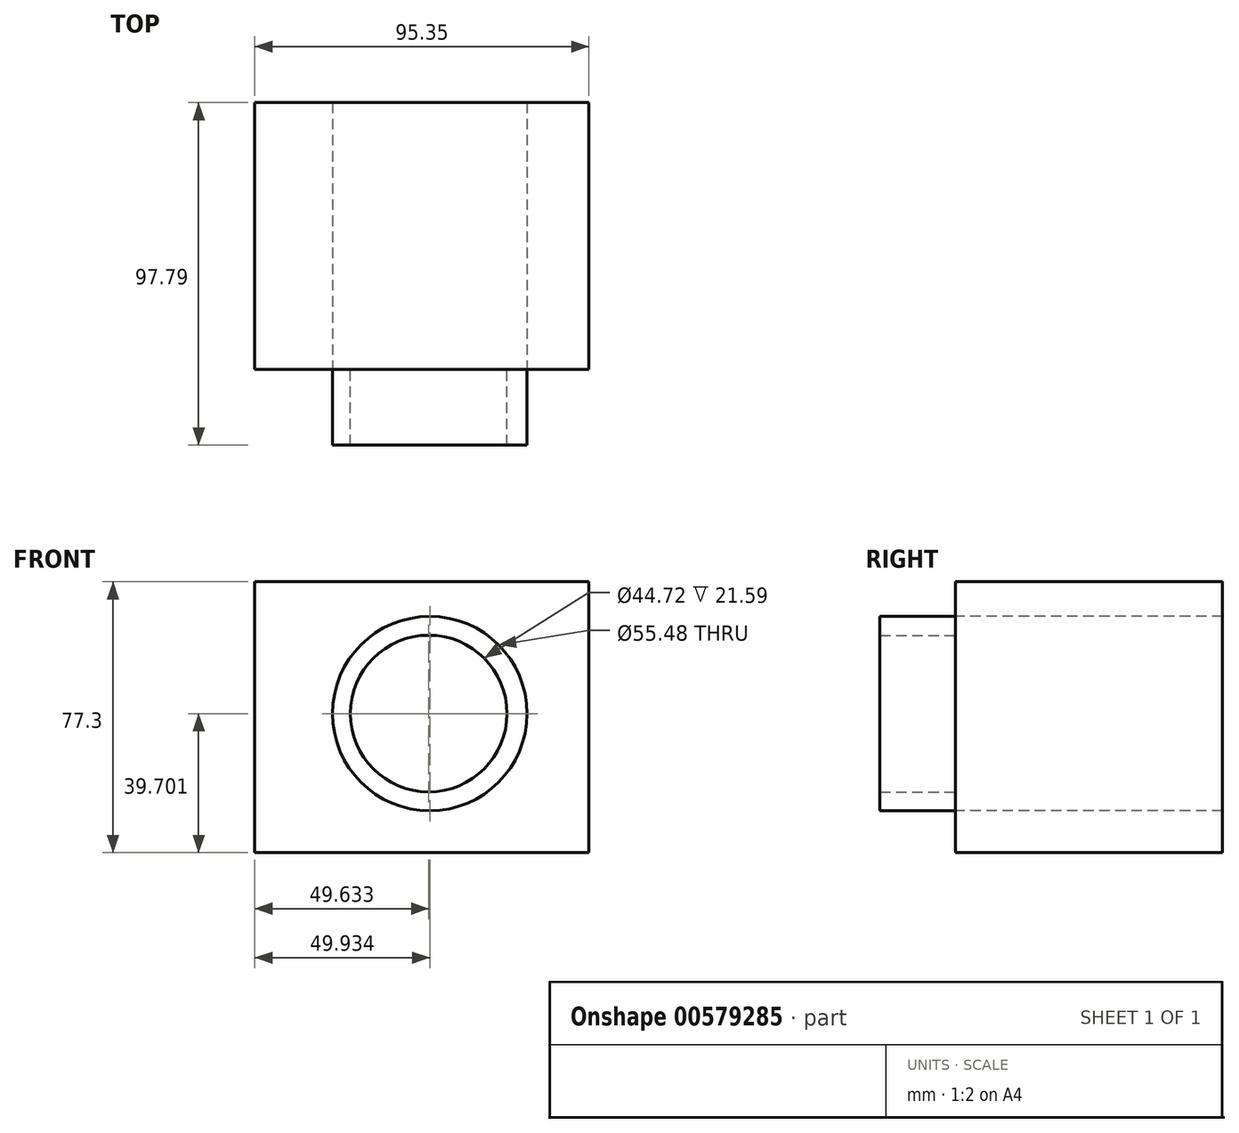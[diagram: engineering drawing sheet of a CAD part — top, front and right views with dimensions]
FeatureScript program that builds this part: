
annotation { "Feature Type Name" : "Feature", "Feature Type Description" : "" }
export const myFeature = defineFeature(function(context is Context, id is Id, definition is map)
    precondition{}
    {
        {
            var Q0;
            Q0=qCreatedBy(makeId("Front.planeOp"),FACE);
            var sketch = newSketch(context, id + "F0", { "sketchPlane" : qUnion([Q0])});
            skLineSegment(sketch, "E0.bottom", {"start": v(-44.52, 33.99) * mm, "end": v(50.83, 33.99) * mm});
            skLineSegment(sketch, "E0.top", {"start": v(-44.52, -43.31) * mm, "end": v(50.83, -43.31) * mm});
            skLineSegment(sketch, "E0.left", {"start": v(-44.52, 33.99) * mm, "end": v(-44.52, -43.31) * mm});
            skLineSegment(sketch, "E0.right", {"start": v(50.83, 33.99) * mm, "end": v(50.83, -43.31) * mm});
            skSolve(sketch);
        }
        {
            var Q0;
            Q0=makeQuery(id+"F0.imprint","IMPRINT",FACE,{"disambiguationData":[TD([[makeQuery(id+"F0.imprint","IMPRINT",EDGE,{"derivedFrom":sQuery(id+"F0.wireOp",EDGE,"E0.bottom")}),-1.0]])]});
            extrude(context, id + "F1", {"entities" : qUnion([Q0]), "depth" : 76.2 * mm, "offsetDistance" : 25.4 * mm});
        }
        {
            var Q0;
            Q0=makeQuery(id+"F1.opExtrude","CAP_FACE",FACE,{"disambiguationData":[OSD([sQuery(id+"F0.wireOp",EDGE,"E0.bottom"),sQuery(id+"F0.wireOp",EDGE,"E0.top"),sQuery(id+"F0.wireOp",EDGE,"E0.left"),sQuery(id+"F0.wireOp",EDGE,"E0.right")])],"isStart":false});
            var sketch = newSketch(context, id + "F2", { "sketchPlane" : qUnion([Q0])});
            skCircle(sketch, "E1", {"center": v(5.41, -3.6) * mm, "radius": 27.74 * mm});
            skSolve(sketch);
        }
        {
            var Q0;
            Q0=makeQuery(id+"F2.imprint","IMPRINT",FACE,{"disambiguationData":[TD([[makeQuery(id+"F2.imprint","IMPRINT",EDGE,{"derivedFrom":sQuery(id+"F2.wireOp",EDGE,"E1")}),1.0]])]});
            var sketch = newSketch(context, id + "F3", { "sketchPlane" : qUnion([Q0])});
            skCircle(sketch, "E2", {"center": v(5.11, -3.6) * mm, "radius": 22.36 * mm});
            skSolve(sketch);
        }
        {
            var Q0;
            Q0=makeQuery(id+"F3.imprint","IMPRINT",FACE,{"disambiguationData":[TD([[makeQuery(id+"F3.imprint","IMPRINT",EDGE,{"derivedFrom":sQuery(id+"F3.wireOp",EDGE,"E2")}),-1.0]])]});
            extrude(context, id + "F4", {"entities" : qUnion([Q0]), "operationType" : NewBodyOperationType.ADD, "endBound" : BoundingType.SYMMETRIC, "depth" : 43.18 * mm, "offsetDistance" : 25.4 * mm});
        }
        {
            var Q0;
            Q0=makeQuery(id+"F2.imprint","IMPRINT",FACE,{"disambiguationData":[TD([[makeQuery(id+"F2.imprint","IMPRINT",EDGE,{"derivedFrom":sQuery(id+"F2.wireOp",EDGE,"E1")}),1.0]])]});
            extrude(context, id + "F5", {"entities" : qUnion([Q0]), "operationType" : NewBodyOperationType.REMOVE, "endBound" : BoundingType.THROUGH_ALL, "oppositeDirection" : true, "depth" : 254 * mm, "offsetDistance" : 25.4 * mm});
        }
    });
